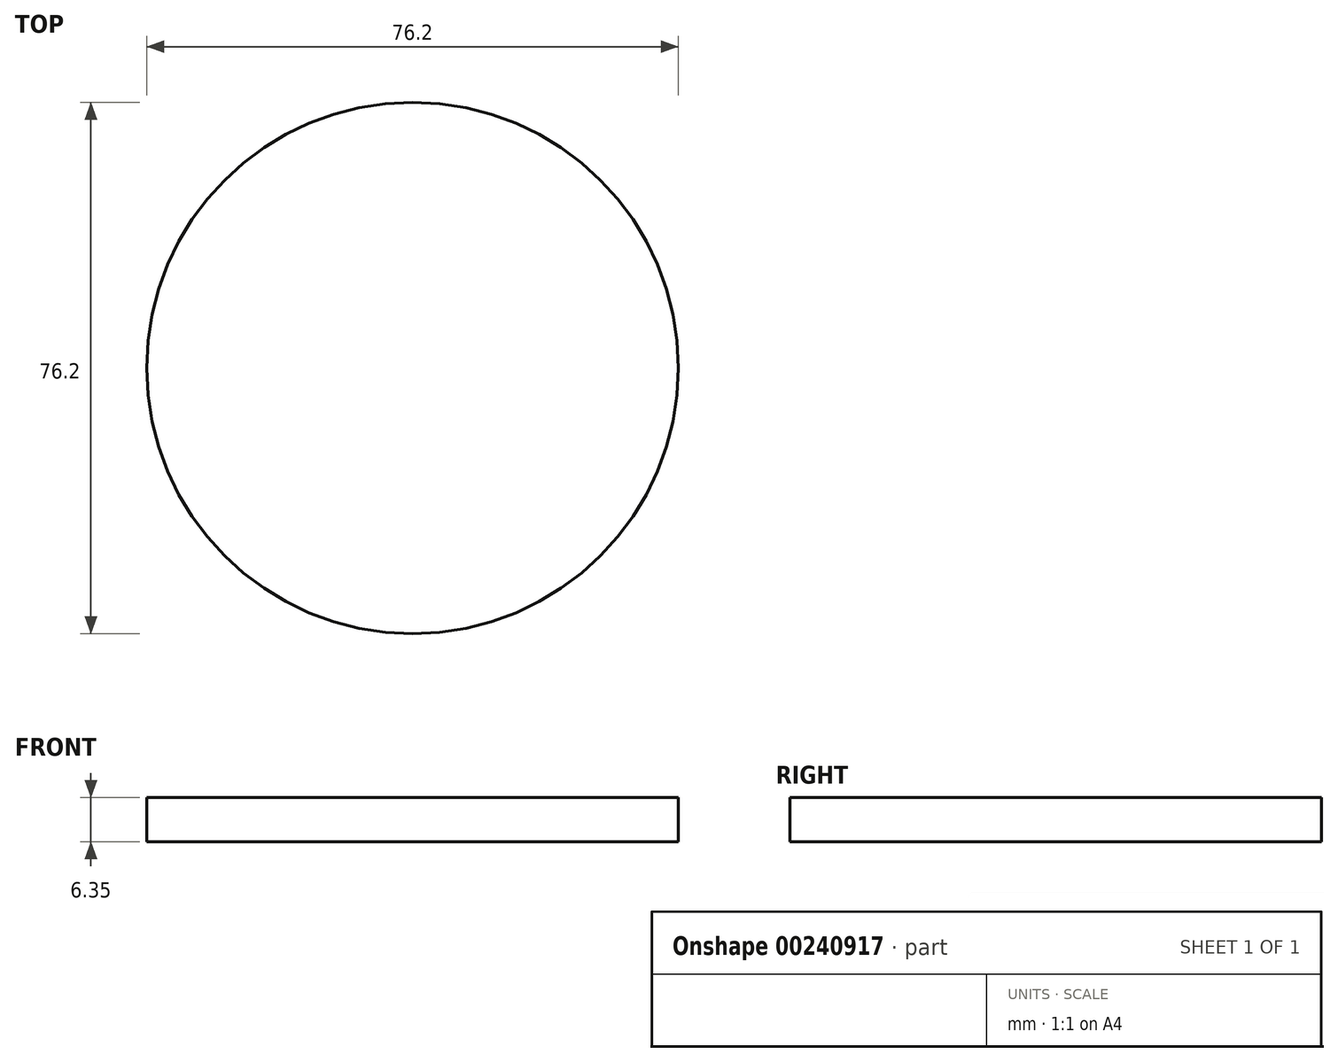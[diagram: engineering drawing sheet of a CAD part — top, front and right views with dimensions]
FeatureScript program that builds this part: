
annotation { "Feature Type Name" : "Feature", "Feature Type Description" : "" }
export const myFeature = defineFeature(function(context is Context, id is Id, definition is map)
    precondition{}
    {
        {
            var Q0;
            Q0=qCreatedBy(makeId("Top.planeOp"),FACE);
            var sketch = newSketch(context, id + "F0", { "sketchPlane" : qUnion([Q0])});
            skCircle(sketch, "E0", {"center": v(0, 0) * mm, "radius": 38.1 * mm});
            skSolve(sketch);
        }
        {
            var Q0;
            Q0=makeQuery(id+"F0.imprint","IMPRINT",FACE,{"disambiguationData":[TD([[makeQuery(id+"F0.imprint","IMPRINT",EDGE,{"derivedFrom":sQuery(id+"F0.wireOp",EDGE,"E0")}),1.0]])]});
            extrude(context, id + "F1", {"entities" : qUnion([Q0]), "depth" : 6.35 * mm});
        }
    });
